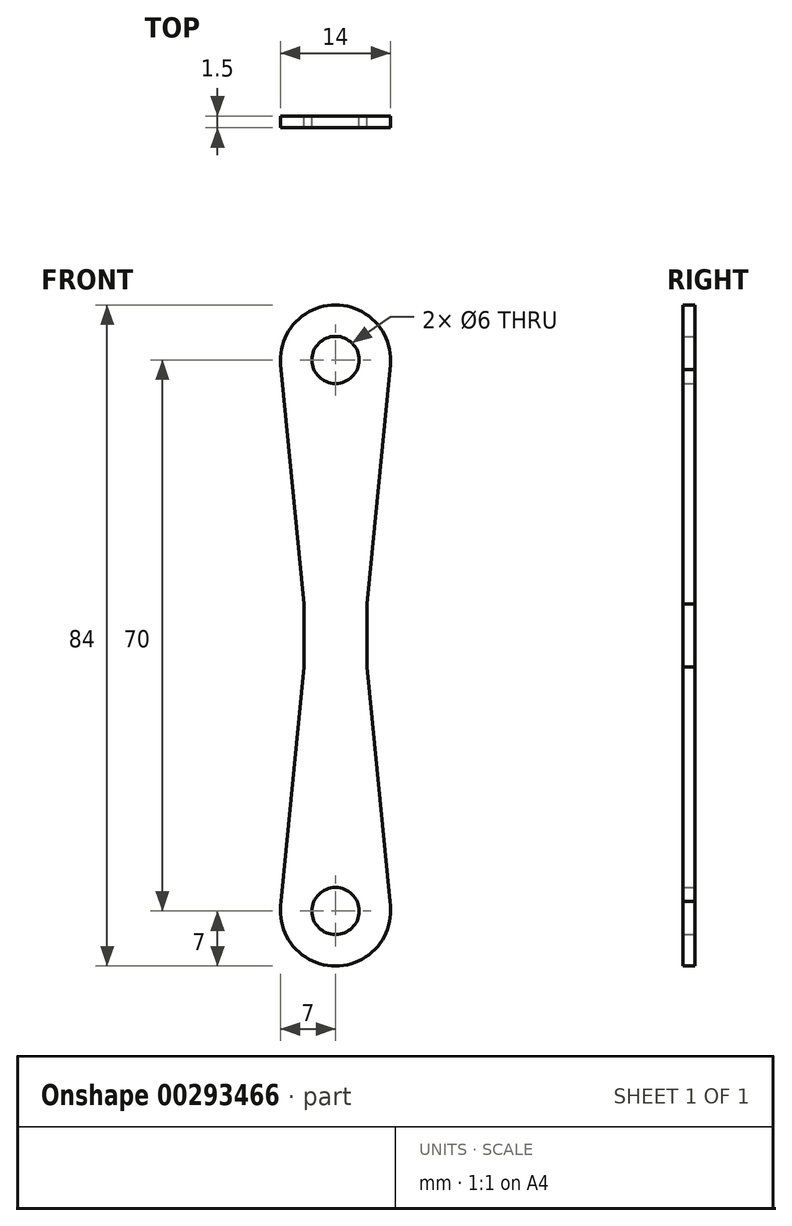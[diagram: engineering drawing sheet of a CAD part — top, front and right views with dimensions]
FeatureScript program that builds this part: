
annotation { "Feature Type Name" : "Feature", "Feature Type Description" : "" }
export const myFeature = defineFeature(function(context is Context, id is Id, definition is map)
    precondition{}
    {
        {
            var Q0;
            Q0=qCreatedBy(makeId("Front.planeOp"),FACE);
            var sketch = newSketch(context, id + "F0", { "sketchPlane" : qUnion([Q0])});
            skLineSegment(sketch, "E0", {"start": v(0, -28.88) * mm, "end": v(0, 46.24) * mm, "construction": true});
            skArc(sketch, "E1", {"start": v(-6.9, 1.2) * mm, "mid": v(-5.35, -4.5) * mm, "end": v(0, -7) * mm});
            skArc(sketch, "E2", {"start": v(0, 3) * mm, "mid": v(-3, 0) * mm, "end": v(0, -3) * mm});
            skLineSegment(sketch, "E3", {"start": v(-19.47, 35) * mm, "end": v(30.4, 35) * mm, "construction": true});
            skLineSegment(sketch, "E4", {"start": v(-4, 35) * mm, "end": v(-4, 31) * mm});
            skLineSegment(sketch, "E5", {"start": v(-4, 31) * mm, "end": v(-6.9, 1.2) * mm});
            skLineSegment(sketch, "E6.MirrorCS", {"start": v(4, 35) * mm, "end": v(4, 31) * mm});
            skLineSegment(sketch, "E7.MirrorCS", {"start": v(4, 31) * mm, "end": v(6.9, 1.2) * mm});
            skArc(sketch, "E8.MirrorCS", {"start": v(0, 3) * mm, "mid": v(3, 0) * mm, "end": v(0, -3) * mm});
            skArc(sketch, "E9.MirrorCS", {"start": v(6.9, 1.2) * mm, "mid": v(5.35, -4.5) * mm, "end": v(0, -7) * mm});
            skLineSegment(sketch, "E10.MirrorCS", {"start": v(-4, 35) * mm, "end": v(-4, 39) * mm});
            skLineSegment(sketch, "E11.MirrorCS", {"start": v(4, 35) * mm, "end": v(4, 39) * mm});
            skLineSegment(sketch, "E12.MirrorCS", {"start": v(4, 39) * mm, "end": v(6.9, 68.8) * mm});
            skLineSegment(sketch, "E13.MirrorCS", {"start": v(-4, 39) * mm, "end": v(-6.9, 68.8) * mm});
            skArc(sketch, "E14.MirrorCS", {"start": v(0, 67) * mm, "mid": v(-3, 70) * mm, "end": v(0, 73) * mm});
            skArc(sketch, "E15.MirrorCS", {"start": v(0, 67) * mm, "mid": v(3, 70) * mm, "end": v(0, 73) * mm});
            skArc(sketch, "E16.MirrorCS", {"start": v(6.9, 68.8) * mm, "mid": v(5.35, 74.5) * mm, "end": v(0, 77) * mm});
            skArc(sketch, "E17.MirrorCS", {"start": v(-6.9, 68.8) * mm, "mid": v(-5.35, 74.5) * mm, "end": v(0, 77) * mm});
            skSolve(sketch);
        }
        {
            var Q0;
            Q0=makeQuery(id+"F0.imprint","IMPRINT",FACE,{"disambiguationData":[TD([[makeQuery(id+"F0.imprint","IMPRINT",EDGE,{"derivedFrom":sQuery(id+"F0.wireOp",EDGE,"E1")}),1.0]])]});
            extrude(context, id + "F1", {"entities" : qUnion([Q0]), "depth" : 1.5 * mm});
        }
    });
